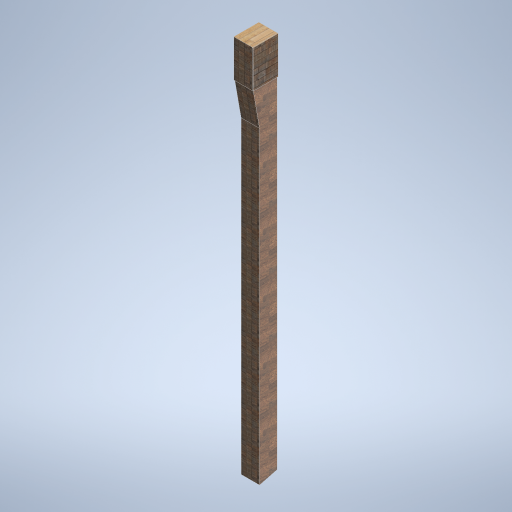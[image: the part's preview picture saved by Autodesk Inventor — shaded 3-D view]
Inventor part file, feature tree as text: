
AUTODESK INVENTOR PART (.ipt)
format: ipt  version: 2024.2 (Build 282272000, 272)  size: 320,512 bytes
history: native  units: in
note: dims shown in document units (in); Inventor stores cm internally (conversion verified against a paired STEP export)
features: other x3, sketch x1
ambient origin geometry x8: Origin, YZ Plane, XZ Plane, XY Plane, X Axis, Y Axis, Z Axis, Center Point
bodies: Solid1 (feature_tree)
feature tree (4):
  other  "side_pillar_02.ipt"
  other  "Solid1::side_pillar_02.ipt"
  other  "TaggingFeature1"
  sketch  "Sketch3"  dims[d0=0.3937in]
